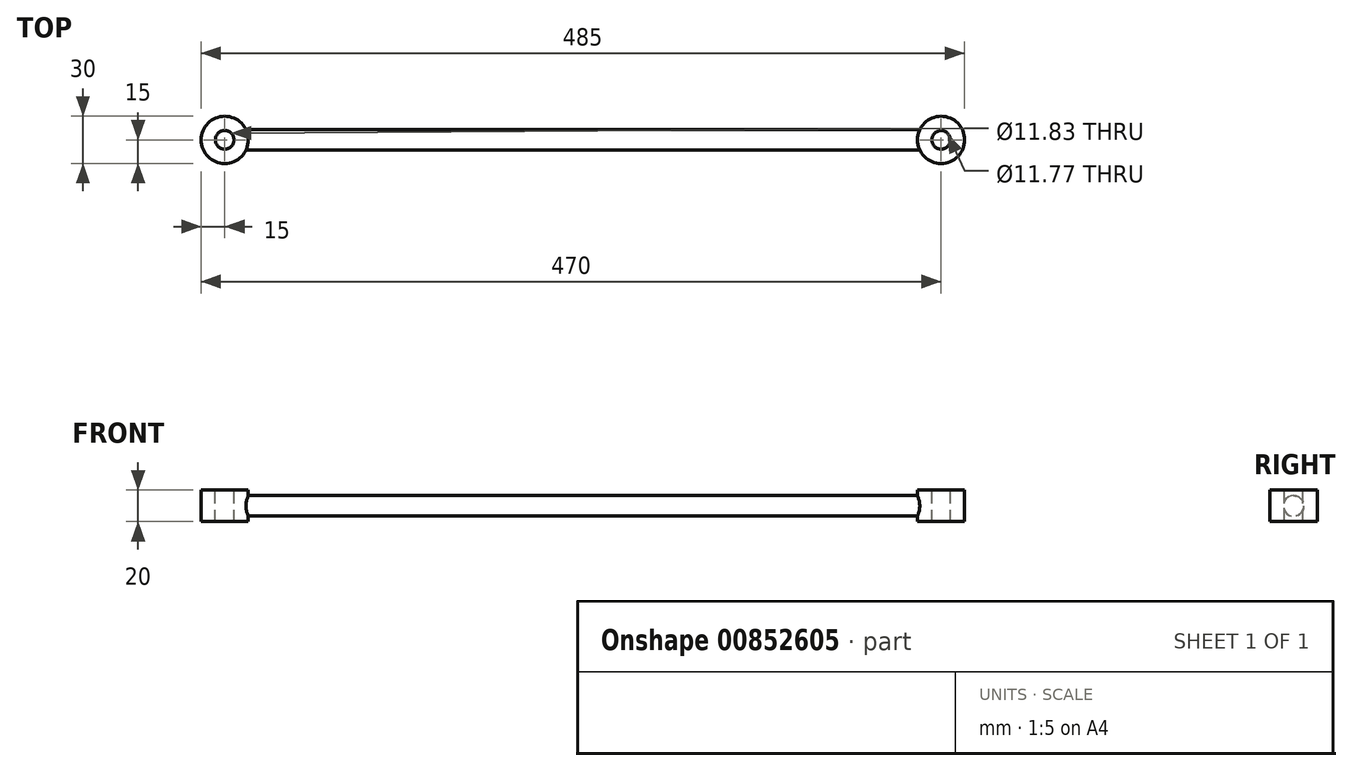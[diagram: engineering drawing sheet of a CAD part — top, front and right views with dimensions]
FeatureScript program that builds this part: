
annotation { "Feature Type Name" : "Feature", "Feature Type Description" : "" }
export const myFeature = defineFeature(function(context is Context, id is Id, definition is map)
    precondition{}
    {
        {
            var Q0;
            Q0=qCreatedBy(makeId("Top.planeOp"),FACE);
            var sketch = newSketch(context, id + "F0", { "sketchPlane" : qUnion([Q0])});
            skCircle(sketch, "E0", {"center": v(-227.5, 0) * mm, "radius": 15 * mm});
            skCircle(sketch, "E1", {"center": v(227.5, 0) * mm, "radius": 15 * mm});
            skCircle(sketch, "E2", {"center": v(-227.5, 0) * mm, "radius": 5.91 * mm});
            skCircle(sketch, "E3", {"center": v(227.5, 0) * mm, "radius": 5.88 * mm});
            skSolve(sketch);
        }
        {
            var Q0;
            Q0=makeQuery(id+"F0.imprint","IMPRINT",FACE,{"disambiguationData":[TD([[makeQuery(id+"F0.imprint","IMPRINT",EDGE,{"derivedFrom":sQuery(id+"F0.wireOp",EDGE,"E0")}),1.0]])]});
            var Q1;
            Q1=makeQuery(id+"F0.imprint","IMPRINT",FACE,{"disambiguationData":[TD([[makeQuery(id+"F0.imprint","IMPRINT",EDGE,{"derivedFrom":sQuery(id+"F0.wireOp",EDGE,"E1")}),1.0]])]});
            extrude(context, id + "F1", {"entities" : qUnion([Q0, Q1]), "oppositeDirection" : true, "depth" : 20 * mm, "offsetDistance" : 25 * mm, "symmetric" : true});
        }
        {
            var Q0;
            Q0=qCreatedBy(makeId("Right.planeOp"),FACE);
            var sketch = newSketch(context, id + "F2", { "sketchPlane" : qUnion([Q0])});
            skCircle(sketch, "E4", {"center": v(0, 0) * mm, "radius": 6.5 * mm});
            skSolve(sketch);
        }
        {
            var Q0;
            Q0=makeQuery(id+"F2.imprint","IMPRINT",FACE,{"disambiguationData":[TD([[makeQuery(id+"F2.imprint","IMPRINT",EDGE,{"derivedFrom":sQuery(id+"F2.wireOp",EDGE,"E4")}),1.0]])]});
            extrude(context, id + "F3", {"entities" : qUnion([Q0]), "operationType" : NewBodyOperationType.ADD, "depth" : 431.37 * mm, "offsetDistance" : 25 * mm, "symmetric" : true});
        }
    });
